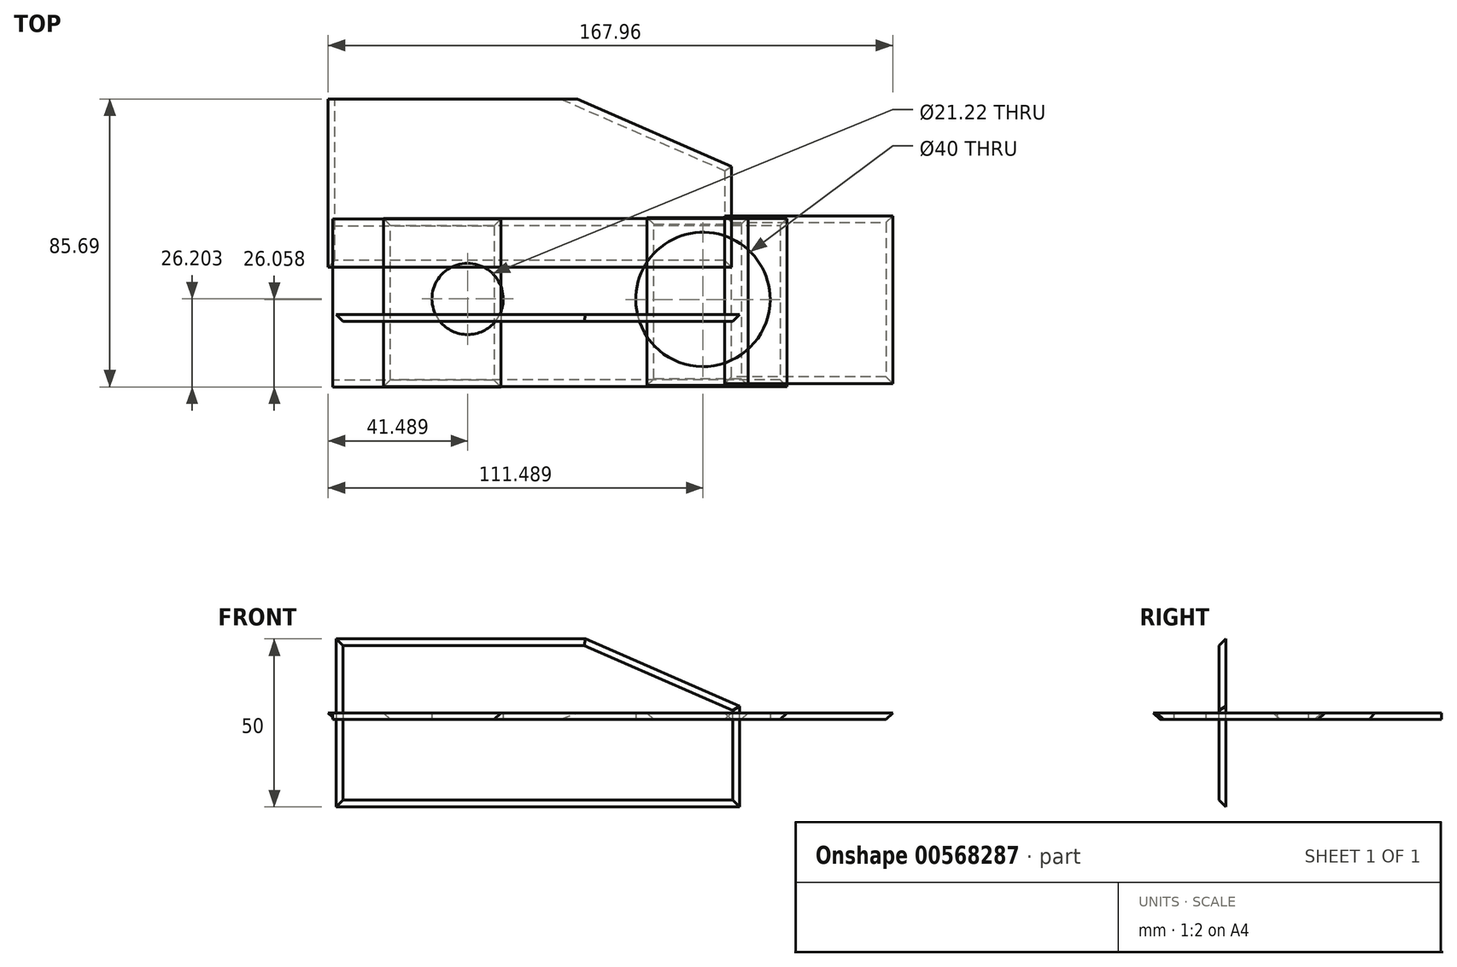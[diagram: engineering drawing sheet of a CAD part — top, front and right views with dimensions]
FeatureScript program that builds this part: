
annotation { "Feature Type Name" : "Feature", "Feature Type Description" : "" }
export const myFeature = defineFeature(function(context is Context, id is Id, definition is map)
    precondition{}
    {
        {
            var Q0;
            Q0=qCreatedBy(makeId("Top.planeOp"),FACE);
            var sketch = newSketch(context, id + "F0", { "sketchPlane" : qUnion([Q0])});
            skLineSegment(sketch, "E0.bottom", {"start": v(-48.73, 28.54) * mm, "end": v(71.27, 28.54) * mm});
            skLineSegment(sketch, "E0.top", {"start": v(-48.73, -21.46) * mm, "end": v(71.27, -21.46) * mm});
            skLineSegment(sketch, "E0.left", {"start": v(-48.73, 28.54) * mm, "end": v(-48.73, -21.46) * mm});
            skLineSegment(sketch, "E0.right", {"start": v(71.27, 28.54) * mm, "end": v(71.27, -21.46) * mm});
            skCircle(sketch, "E1", {"center": v(-23.73, 4.67) * mm, "radius": 10.6 * mm});
            skCircle(sketch, "E2", {"center": v(46.27, 4.53) * mm, "radius": 20 * mm});
            skSolve(sketch);
        }
        {
            var Q0;
            Q0 = qSketchRegion(id + "F0", true);
            extrude(context, id + "F1", {"entities" : qUnion([Q0]), "depth" : 2 * mm, "offsetDistance" : 25 * mm});
        }
        {
            var Q0;
            Q0=qCreatedBy(makeId("Top.planeOp"),FACE);
            var sketch = newSketch(context, id + "F2", { "sketchPlane" : qUnion([Q0])});
            skLineSegment(sketch, "E3.bottom", {"start": v(-13.87, 28.47) * mm, "end": v(-63.87, 28.47) * mm});
            skLineSegment(sketch, "E3.top", {"start": v(-13.87, -21.53) * mm, "end": v(-63.87, -21.53) * mm});
            skLineSegment(sketch, "E3.left", {"start": v(-13.87, 28.47) * mm, "end": v(-13.87, -21.53) * mm});
            skLineSegment(sketch, "E3.right", {"start": v(-63.87, 28.47) * mm, "end": v(-63.87, -21.53) * mm});
            skSolve(sketch);
        }
        {
            var Q0;
            Q0 = qSketchRegion(id + "F2", true);
            extrude(context, id + "F3", {"entities" : qUnion([Q0]), "depth" : 2 * mm, "offsetDistance" : 25 * mm});
        }
        {
            var Q0;
            Q0=qCreatedBy(makeId("Top.planeOp"),FACE);
            var sketch = newSketch(context, id + "F4", { "sketchPlane" : qUnion([Q0])});
            skLineSegment(sketch, "E4.bottom", {"start": v(29.66, -21.09) * mm, "end": v(59.66, -21.09) * mm});
            skLineSegment(sketch, "E4.top", {"start": v(29.66, 28.91) * mm, "end": v(59.66, 28.91) * mm});
            skLineSegment(sketch, "E4.left", {"start": v(29.66, -21.09) * mm, "end": v(29.66, 28.91) * mm});
            skLineSegment(sketch, "E4.right", {"start": v(59.66, -21.09) * mm, "end": v(59.66, 28.91) * mm});
            skSolve(sketch);
        }
        {
            var Q0;
            Q0 = qSketchRegion(id + "F4", true);
            extrude(context, id + "F5", {"entities" : qUnion([Q0]), "depth" : 2 * mm, "offsetDistance" : 25 * mm});
        }
        {
            var Q0;
            Q0=qCreatedBy(makeId("Top.planeOp"),FACE);
            var sketch = newSketch(context, id + "F6", { "sketchPlane" : qUnion([Q0])});
            skLineSegment(sketch, "E5.bottom", {"start": v(52.74, 29.43) * mm, "end": v(102.74, 29.43) * mm});
            skLineSegment(sketch, "E5.top", {"start": v(52.74, -20.57) * mm, "end": v(102.74, -20.57) * mm});
            skLineSegment(sketch, "E5.left", {"start": v(52.74, 29.43) * mm, "end": v(52.74, -20.57) * mm});
            skLineSegment(sketch, "E5.right", {"start": v(102.74, 29.43) * mm, "end": v(102.74, -20.57) * mm});
            skSolve(sketch);
        }
        {
            var Q0;
            Q0 = qSketchRegion(id + "F6", true);
            extrude(context, id + "F7", {"entities" : qUnion([Q0]), "depth" : 2 * mm, "offsetDistance" : 25 * mm});
        }
        {
            var Q0;
            Q0=qCreatedBy(makeId("Top.planeOp"),FACE);
            var sketch = newSketch(context, id + "F8", { "sketchPlane" : qUnion([Q0])});
            skLineSegment(sketch, "E6", {"start": v(-65.22, 14.16) * mm, "end": v(54.78, 14.16) * mm});
            skLineSegment(sketch, "E7", {"start": v(54.78, 14.16) * mm, "end": v(54.78, 44.16) * mm});
            skLineSegment(sketch, "E8", {"start": v(54.78, 44.16) * mm, "end": v(8.96, 64.16) * mm});
            skLineSegment(sketch, "E9", {"start": v(8.96, 64.16) * mm, "end": v(-65.22, 64.16) * mm});
            skLineSegment(sketch, "E10", {"start": v(-65.22, 64.16) * mm, "end": v(-65.22, 14.16) * mm});
            skSolve(sketch);
        }
        {
            var Q0;
            Q0=makeQuery(id+"F8.imprint","IMPRINT",FACE,{"disambiguationData":[TD([[makeQuery(id+"F8.imprint","IMPRINT",EDGE,{"derivedFrom":sQuery(id+"F8.wireOp",EDGE,"E6")}),1.0]])]});
            extrude(context, id + "F9", {"entities" : qUnion([Q0]), "depth" : 2 * mm, "offsetDistance" : 25 * mm});
        }
        {
            var Q0;
            Q0=qCreatedBy(makeId("Front.planeOp"),FACE);
            var sketch = newSketch(context, id + "F10", { "sketchPlane" : qUnion([Q0])});
            skLineSegment(sketch, "E11", {"start": v(-62.83, -26) * mm, "end": v(57.17, -26) * mm});
            skLineSegment(sketch, "E12", {"start": v(57.17, -26) * mm, "end": v(57.17, 4) * mm});
            skLineSegment(sketch, "E13", {"start": v(57.17, 4) * mm, "end": v(11.34, 24) * mm});
            skLineSegment(sketch, "E14", {"start": v(11.34, 24) * mm, "end": v(-62.83, 24) * mm});
            skLineSegment(sketch, "E15", {"start": v(-62.83, 24) * mm, "end": v(-62.83, -26) * mm});
            skSolve(sketch);
        }
        {
            var Q0;
            Q0 = qSketchRegion(id + "F10", true);
            var Q1;
            Q1=makeQuery(id+"F10.imprint","IMPRINT",FACE,{"disambiguationData":[TD([[makeQuery(id+"F10.imprint","IMPRINT",EDGE,{"derivedFrom":sQuery(id+"F10.wireOp",EDGE,"E11")}),1.0]])]});
            extrude(context, id + "F11", {"entities" : qUnion([Q0, Q1]), "depth" : 2 * mm, "offsetDistance" : 25 * mm});
        }
        {
            var Q0;
            Q0=makeQuery(id+"F1.opExtrude","CAP_EDGE",EDGE,{"disambiguationData":[OSD([sQuery(id+"F0.wireOp",EDGE,"E0.right")])],"isStart":true});
            var Q1;
            Q1=makeQuery(id+"F1.opExtrude","CAP_EDGE",EDGE,{"disambiguationData":[OSD([sQuery(id+"F0.wireOp",EDGE,"E0.bottom")])],"isStart":true});
            var Q2;
            Q2=makeQuery(id+"F1.opExtrude","CAP_EDGE",EDGE,{"disambiguationData":[OSD([sQuery(id+"F0.wireOp",EDGE,"E0.left")])],"isStart":true});
            var Q3;
            Q3=makeQuery(id+"F1.opExtrude","CAP_EDGE",EDGE,{"disambiguationData":[OSD([sQuery(id+"F0.wireOp",EDGE,"E0.top")])],"isStart":true});
            chamfer(context, id + "F12", {"entities" : qUnion([Q0, Q1, Q2, Q3]), "width" : 2 * mm, "tangentPropagation" : true});
        }
        {
            var Q0;
            Q0=makeQuery(id+"F3.opExtrude","CAP_EDGE",EDGE,{"disambiguationData":[OSD([sQuery(id+"F2.wireOp",EDGE,"E3.top")])],"isStart":true});
            var Q1;
            Q1=makeQuery(id+"F3.opExtrude","CAP_EDGE",EDGE,{"disambiguationData":[OSD([sQuery(id+"F2.wireOp",EDGE,"E3.left")])],"isStart":true});
            var Q2;
            Q2=makeQuery(id+"F3.opExtrude","CAP_EDGE",EDGE,{"disambiguationData":[OSD([sQuery(id+"F2.wireOp",EDGE,"E3.bottom")])],"isStart":true});
            chamfer(context, id + "F13", {"entities" : qUnion([Q0, Q1, Q2]), "width" : 2 * mm, "tangentPropagation" : true});
        }
        {
            var Q0;
            Q0=makeQuery(id+"F5.opExtrude","CAP_EDGE",EDGE,{"disambiguationData":[OSD([sQuery(id+"F4.wireOp",EDGE,"E4.bottom")])],"isStart":true});
            var Q1;
            Q1=makeQuery(id+"F5.opExtrude","CAP_EDGE",EDGE,{"disambiguationData":[OSD([sQuery(id+"F4.wireOp",EDGE,"E4.left")])],"isStart":true});
            var Q2;
            Q2=makeQuery(id+"F5.opExtrude","CAP_EDGE",EDGE,{"disambiguationData":[OSD([sQuery(id+"F4.wireOp",EDGE,"E4.top")])],"isStart":true});
            var Q3;
            Q3=makeQuery(id+"F5.opExtrude","CAP_EDGE",EDGE,{"disambiguationData":[OSD([sQuery(id+"F4.wireOp",EDGE,"E4.right")])],"isStart":true});
            chamfer(context, id + "F14", {"entities" : qUnion([Q0, Q1, Q2, Q3]), "width" : 2 * mm, "tangentPropagation" : true});
        }
        {
            var Q0;
            Q0=makeQuery(id+"F7.opExtrude","CAP_EDGE",EDGE,{"disambiguationData":[OSD([sQuery(id+"F6.wireOp",EDGE,"E5.top")])],"isStart":true});
            var Q1;
            Q1=makeQuery(id+"F7.opExtrude","CAP_EDGE",EDGE,{"disambiguationData":[OSD([sQuery(id+"F6.wireOp",EDGE,"E5.left")])],"isStart":true});
            var Q2;
            Q2=makeQuery(id+"F7.opExtrude","CAP_EDGE",EDGE,{"disambiguationData":[OSD([sQuery(id+"F6.wireOp",EDGE,"E5.bottom")])],"isStart":true});
            var Q3;
            Q3=makeQuery(id+"F7.opExtrude","CAP_EDGE",EDGE,{"disambiguationData":[OSD([sQuery(id+"F6.wireOp",EDGE,"E5.right")])],"isStart":true});
            chamfer(context, id + "F15", {"entities" : qUnion([Q0, Q1, Q2, Q3]), "width" : 2 * mm, "tangentPropagation" : true});
        }
        {
            var Q0;
            Q0=makeQuery(id+"F9.opExtrude","CAP_EDGE",EDGE,{"disambiguationData":[OSD([sQuery(id+"F8.wireOp",EDGE,"E6")])],"isStart":true});
            var Q1;
            Q1=makeQuery(id+"F9.opExtrude","CAP_EDGE",EDGE,{"disambiguationData":[OSD([sQuery(id+"F8.wireOp",EDGE,"E10")])],"isStart":true});
            var Q2;
            Q2=makeQuery(id+"F9.opExtrude","CAP_EDGE",EDGE,{"disambiguationData":[OSD([sQuery(id+"F8.wireOp",EDGE,"E7")])],"isStart":true});
            var Q3;
            Q3=makeQuery(id+"F9.opExtrude","CAP_EDGE",EDGE,{"disambiguationData":[OSD([sQuery(id+"F8.wireOp",EDGE,"E8")])],"isStart":true});
            chamfer(context, id + "F16", {"entities" : qUnion([Q0, Q1, Q2, Q3]), "width" : 2 * mm, "tangentPropagation" : true});
        }
        {
            var Q0;
            Q0=makeQuery(id+"F11.opExtrude","CAP_EDGE",EDGE,{"disambiguationData":[OSD([sQuery(id+"F10.wireOp",EDGE,"E13")])],"isStart":false});
            var Q1;
            Q1=makeQuery(id+"F11.opExtrude","CAP_EDGE",EDGE,{"disambiguationData":[OSD([sQuery(id+"F10.wireOp",EDGE,"E14")])],"isStart":false});
            var Q2;
            Q2=makeQuery(id+"F11.opExtrude","CAP_EDGE",EDGE,{"disambiguationData":[OSD([sQuery(id+"F10.wireOp",EDGE,"E15")])],"isStart":false});
            var Q3;
            Q3=makeQuery(id+"F11.opExtrude","CAP_EDGE",EDGE,{"disambiguationData":[OSD([sQuery(id+"F10.wireOp",EDGE,"E12")])],"isStart":false});
            var Q4;
            Q4=makeQuery(id+"F11.opExtrude","CAP_EDGE",EDGE,{"disambiguationData":[OSD([sQuery(id+"F10.wireOp",EDGE,"E11")])],"isStart":false});
            chamfer(context, id + "F17", {"entities" : qUnion([Q0, Q1, Q2, Q3, Q4]), "width" : 2 * mm, "tangentPropagation" : true});
        }
    });
